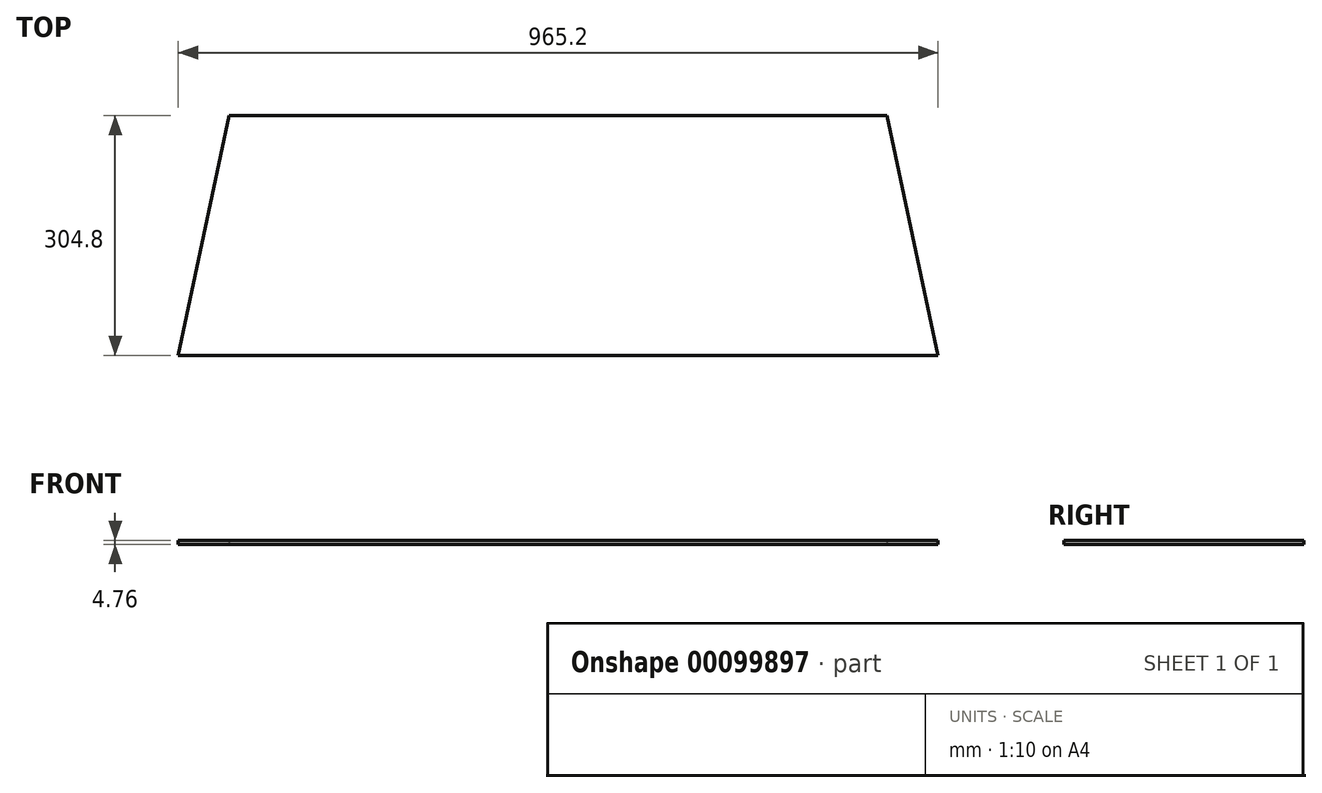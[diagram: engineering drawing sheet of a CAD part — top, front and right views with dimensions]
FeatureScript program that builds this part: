
annotation { "Feature Type Name" : "Feature", "Feature Type Description" : "" }
export const myFeature = defineFeature(function(context is Context, id is Id, definition is map)
    precondition{}
    {
        {
            var Q0;
            Q0=qCreatedBy(makeId("Top.planeOp"),FACE);
            var sketch = newSketch(context, id + "F0", { "sketchPlane" : qUnion([Q0])});
            skLineSegment(sketch, "E0.bottom", {"start": v(417.81, 152.4) * mm, "end": v(-417.81, 152.4) * mm});
            skLineSegment(sketch, "E0.top", {"start": v(482.6, -152.4) * mm, "end": v(-482.6, -152.4) * mm});
            skLineSegment(sketch, "E0.left", {"start": v(482.6, 152.4) * mm, "end": v(482.6, -152.4) * mm});
            skLineSegment(sketch, "E0.right", {"start": v(-482.6, 152.4) * mm, "end": v(-482.6, -152.4) * mm});
            skPoint(sketch, "E0.middle", {"position": v(0, 0) * mm});
            skLineSegment(sketch, "E1", {"start": v(-482.6, -152.4) * mm, "end": v(-417.81, 152.4) * mm});
            skLineSegment(sketch, "E2", {"start": v(482.6, -152.4) * mm, "end": v(417.81, 152.4) * mm});
            skSolve(sketch);
        }
        {
            var Q0;
            Q0 = qSketchRegion(id + "F0", true);
            extrude(context, id + "F1", {"entities" : qUnion([Q0]), "depth" : 4.76 * mm});
        }
    });
